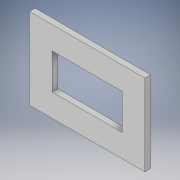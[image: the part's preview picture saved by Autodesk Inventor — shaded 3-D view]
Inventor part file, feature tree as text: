
AUTODESK INVENTOR PART (.ipt)
format: ipt  version: 2017 (Build 210142000, 142)  size: 95,232 bytes
history: native  units: in
note: dims shown in document units (in); Inventor stores cm internally (conversion verified against a paired STEP export)
features: extrude x1, sketch x1
ambient origin geometry x8: Origin, YZ Plane, XZ Plane, XY Plane, X Axis, Y Axis, Z Axis, Center Point
bodies: Solid1 (feature_tree)
feature tree (2):
  extrude  "Extrusion1"  Depth=2.528in
  sketch  "Sketch1"  dims[d0=1.78in d1=2.528in d4=1.528in d5=0.78in d6=0.125in d7=0.0in]
